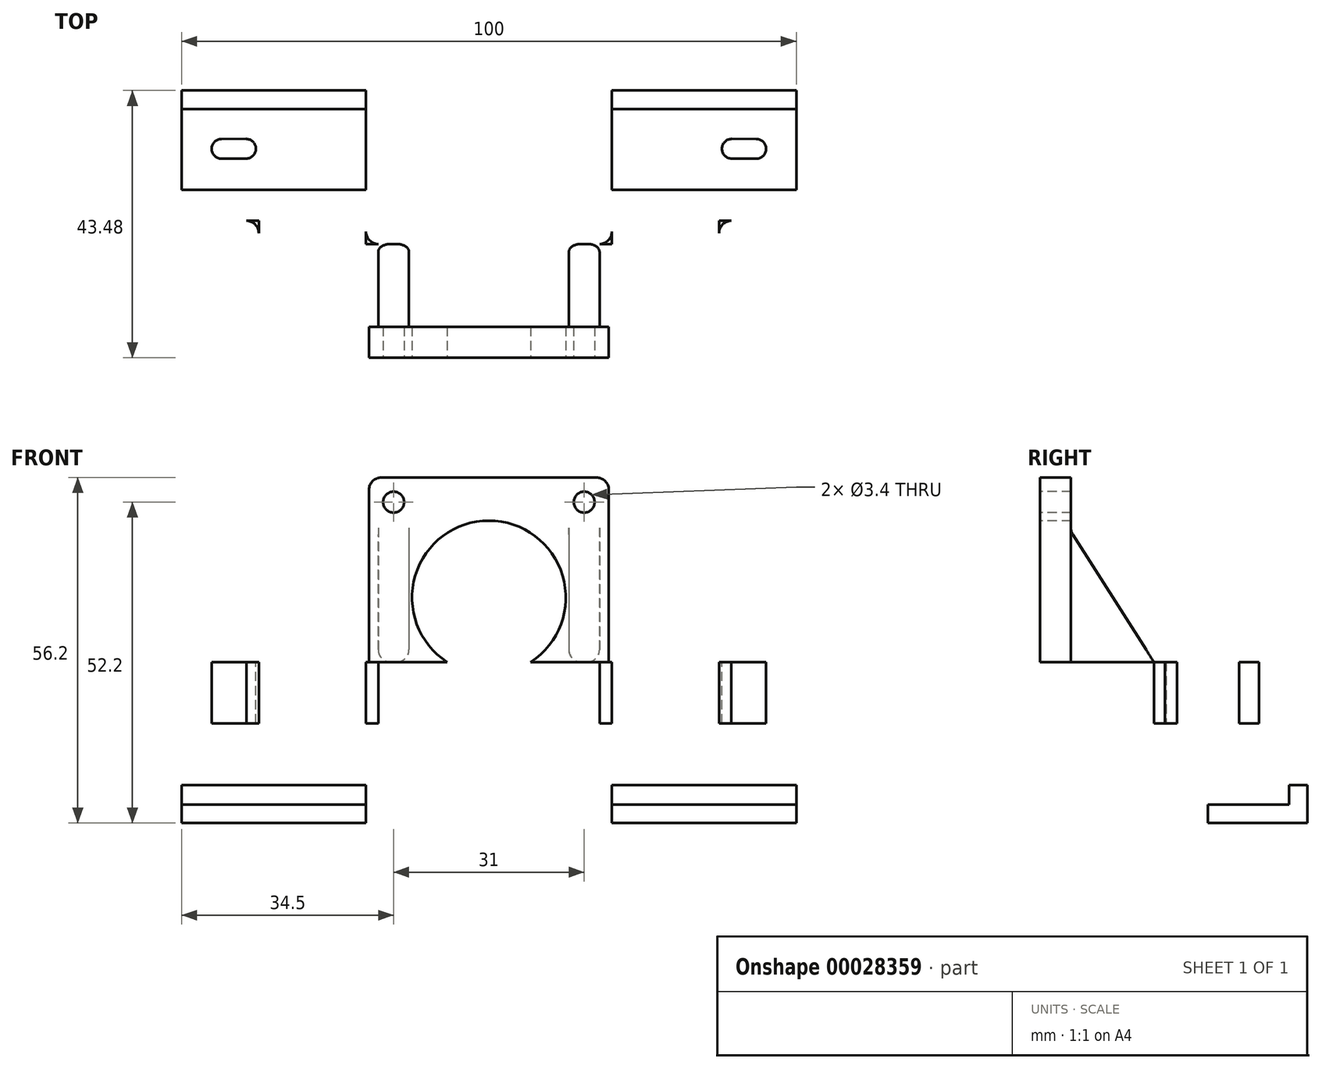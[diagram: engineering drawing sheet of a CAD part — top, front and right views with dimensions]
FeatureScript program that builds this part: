
annotation { "Feature Type Name" : "Feature", "Feature Type Description" : "" }
export const myFeature = defineFeature(function(context is Context, id is Id, definition is map)
    precondition{}
    {
        {
            var Q0;
            Q0=qCreatedBy(makeId("Top.planeOp"),FACE);
            var sketch = newSketch(context, id + "F0", { "sketchPlane" : qUnion([Q0])});
            skLineSegment(sketch, "E0", {"start": v(0, -13.82) * mm, "end": v(-37.44, -13.82) * mm});
            skLineSegment(sketch, "E1", {"start": v(-37.44, -13.82) * mm, "end": v(-37.44, 8.46) * mm});
            skLineSegment(sketch, "E2", {"start": v(-37.44, 8.46) * mm, "end": v(-50, 8.46) * mm});
            skLineSegment(sketch, "E3", {"start": v(-50, 8.46) * mm, "end": v(-50, 13.46) * mm});
            skLineSegment(sketch, "E4", {"start": v(-50, 13.46) * mm, "end": v(-20, 13.46) * mm});
            skLineSegment(sketch, "E5", {"start": v(-20, 13.46) * mm, "end": v(-20, 4.68) * mm});
            skLineSegment(sketch, "E6", {"start": v(-20, 4.68) * mm, "end": v(0, 4.68) * mm});
            skLineSegment(sketch, "E7", {"start": v(0, 4.68) * mm, "end": v(0, -13.82) * mm});
            skLineSegment(sketch, "E8.0", {"start": v(-18.87, 13.46) * mm, "end": v(-18.87, 4.68) * mm, "construction": true});
            skSolve(sketch);
        }
        {
            var Q0;
            Q0=qSketchRegion(id+"F0",true);
            extrude(context, id + "F1", {"entities" : qUnion([Q0]), "depth" : 10 * mm});
        }
        {
            var Q0;
            Q0=makeQuery(id+"F1.opExtrude","SWEPT_FACE",FACE,{"disambiguationData":[OSD([sQuery(id+"F0.wireOp",EDGE,"E0")])]});
            var sketch = newSketch(context, id + "F2", { "sketchPlane" : qUnion([Q0])});
            skLineSegment(sketch, "E9", {"start": v(0, 5) * mm, "end": v(0, 5) * mm});
            skCircle(sketch, "E10", {"center": v(-15.5, 5) * mm, "radius": 1.6 * mm});
            skSolve(sketch);
        }
        {
            var Q0;
            Q0=qSketchRegion(id+"F2",true);
            extrude(context, id + "F3", {"entities" : qUnion([Q0]), "operationType" : NewBodyOperationType.REMOVE, "endBound" : BoundingType.THROUGH_ALL, "oppositeDirection" : true, "depth" : 25 * mm});
        }
        {
            var Q0;
            {var subQ0=makeQuery(id+"F1.opExtrude","CAP_FACE",FACE,{"disambiguationData":[OSD([sQuery(id+"F0.wireOp",EDGE,"E0"),sQuery(id+"F0.wireOp",EDGE,"fd64a43a-5635-4f94-a977-4dd36923accb"),sQuery(id+"F0.wireOp",EDGE,"1334f7d4-4c90-4769-8fa3-fe5f576fb005"),sQuery(id+"F0.wireOp",EDGE,"E1"),sQuery(id+"F0.wireOp",EDGE,"E2"),sQuery(id+"F0.wireOp",EDGE,"E3"),sQuery(id+"F0.wireOp",EDGE,"E4"),sQuery(id+"F0.wireOp",EDGE,"E5"),sQuery(id+"F0.wireOp",EDGE,"E6"),sQuery(id+"F0.wireOp",EDGE,"E7")])],"isStart":false});Q0=makeQuery(id+"F22.boolean.opBoolean","MERGE",FACE,{"derivedFrom":[subQ0,makeQuery(id+"F22.opPattern","COPY",FACE,{"derivedFrom":subQ0,"instanceName":"1"})]});}
            var sketch = newSketch(context, id + "F4", { "sketchPlane" : qUnion([Q0])});
            skCircle(sketch, "E11", {"center": v(-30, 1.46) * mm, "radius": 4.1 * mm});
            skLineSegment(sketch, "E12", {"start": v(-30, 1.46) * mm, "end": v(-30, -13.82) * mm, "construction": true});
            skLineSegment(sketch, "E13.bottom", {"start": v(-30.49, -2.04) * mm, "end": v(-29.51, -2.04) * mm});
            skLineSegment(sketch, "E13.top", {"start": v(-30.49, -14.16) * mm, "end": v(-29.51, -14.16) * mm});
            skLineSegment(sketch, "E13.left", {"start": v(-30.49, -2.04) * mm, "end": v(-30.49, -14.16) * mm});
            skLineSegment(sketch, "E13.right", {"start": v(-29.51, -2.04) * mm, "end": v(-29.51, -14.16) * mm});
            skPoint(sketch, "E14", {"position": v(-30, -2.04) * mm});
            skSolve(sketch);
        }
        {
            var Q0;
            Q0=qSketchRegion(id+"F4",true);
            var Q1;
            {var subQ3=sQuery(id+"F4.wireOp",EDGE,"E13.bottom");Q1=makeQuery(id+"F4.imprint","IMPRINT",FACE,{"disambiguationData":[TD([[makeQuery(id+"F4.imprint","IMPRINT",EDGE,{"derivedFrom":subQ3}),-1.0]])]});}
            extrude(context, id + "F5", {"entities" : qUnion([Q0, Q1]), "operationType" : NewBodyOperationType.REMOVE, "endBound" : BoundingType.THROUGH_ALL, "oppositeDirection" : true, "depth" : 25 * mm});
        }
        {
            var Q0;
            Q0=makeQuery(id+"F1.opExtrude","SWEPT_FACE",FACE,{"disambiguationData":[OSD([sQuery(id+"F0.wireOp",EDGE,"E1")])]});
            var sketch = newSketch(context, id + "F6", { "sketchPlane" : qUnion([Q0])});
            skCircle(sketch, "E15", {"center": v(10.1, 4.98) * mm, "radius": 1.4 * mm});
            skCircle(sketch, "E16", {"center": v(10.1, 4.98) * mm, "radius": 1.7 * mm});
            skSolve(sketch);
        }
        {
            var Q0;
            Q0=makeQuery(id+"F6.imprint","IMPRINT",FACE,{"disambiguationData":[TD([[makeQuery(id+"F6.imprint","IMPRINT",EDGE,{"derivedFrom":sQuery(id+"F6.wireOp",EDGE,"E15")}),1.0]])]});
            extrude(context, id + "F7", {"entities" : qUnion([Q0]), "operationType" : NewBodyOperationType.REMOVE, "oppositeDirection" : true, "depth" : 18 * mm});
        }
        {
            var Q0;
            Q0=makeQuery(id+"F1.opExtrude","CAP_FACE",FACE,{"disambiguationData":[OSD([sQuery(id+"F0.wireOp",EDGE,"E0"),sQuery(id+"F0.wireOp",EDGE,"E1"),sQuery(id+"F0.wireOp",EDGE,"E2"),sQuery(id+"F0.wireOp",EDGE,"E3"),sQuery(id+"F0.wireOp",EDGE,"E4"),sQuery(id+"F0.wireOp",EDGE,"E5"),sQuery(id+"F0.wireOp",EDGE,"E6"),sQuery(id+"F0.wireOp",EDGE,"E7")])],"isStart":false});
            var sketch = newSketch(context, id + "F8", { "sketchPlane" : qUnion([Q0])});
            skLineSegment(sketch, "E17.0", {"start": v(-19.51, -2.61) * mm, "end": v(-19.51, -13.82) * mm, "construction": true});
            skLineSegment(sketch, "E18.bottom", {"start": v(-19.51, -13.82) * mm, "end": v(0, -13.82) * mm});
            skLineSegment(sketch, "E18.top", {"start": v(-19.51, -8.82) * mm, "end": v(0, -8.82) * mm});
            skLineSegment(sketch, "E18.left", {"start": v(-19.51, -13.82) * mm, "end": v(-19.51, -8.82) * mm});
            skLineSegment(sketch, "E18.right", {"start": v(0, -13.82) * mm, "end": v(0, -8.82) * mm});
            skSolve(sketch);
        }
        {
            var Q0;
            Q0=makeQuery(id+"F6.imprint","IMPRINT",FACE,{"disambiguationData":[TD([[makeQuery(id+"F6.imprint","IMPRINT",EDGE,{"derivedFrom":sQuery(id+"F6.wireOp",EDGE,"E15")}),1.0]])]});
            var Q1;
            Q1=makeQuery(id+"F6.imprint","IMPRINT",FACE,{"disambiguationData":[TD([[makeQuery(id+"F6.imprint","IMPRINT",EDGE,{"derivedFrom":sQuery(id+"F6.wireOp",EDGE,"E15")}),-1.0]])]});
            extrude(context, id + "F9", {"entities" : qUnion([Q0, Q1]), "operationType" : NewBodyOperationType.REMOVE, "endBound" : BoundingType.UP_TO_NEXT, "oppositeDirection" : true, "depth" : 25 * mm});
        }
        {
            var Q0;
            Q0=makeQuery(id+"F1.opExtrude","SWEPT_FACE",FACE,{"disambiguationData":[OSD([sQuery(id+"F0.wireOp",EDGE,"E3")])]});
            var sketch = newSketch(context, id + "F10", { "sketchPlane" : qUnion([Q0])});
            skLineSegment(sketch, "E19", {"start": v(-13.46, 0) * mm, "end": v(-26.66, 0) * mm});
            skLineSegment(sketch, "E20", {"start": v(-26.66, 0) * mm, "end": v(-26.66, -13.2) * mm});
            skLineSegment(sketch, "E21", {"start": v(-29.66, -13.2) * mm, "end": v(-29.66, 10) * mm});
            skLineSegment(sketch, "E22", {"start": v(-29.66, 10) * mm, "end": v(-13.46, 10) * mm});
            skLineSegment(sketch, "E23", {"start": v(-26.66, -13.2) * mm, "end": v(-13.46, -13.2) * mm});
            skLineSegment(sketch, "E24", {"start": v(-13.46, -13.2) * mm, "end": v(-13.46, -16.2) * mm});
            skLineSegment(sketch, "E25", {"start": v(-13.46, -16.2) * mm, "end": v(-29.66, -16.2) * mm});
            skLineSegment(sketch, "E26", {"start": v(-29.66, -16.2) * mm, "end": v(-29.66, -13.2) * mm});
            skSolve(sketch);
        }
        {
            var Q0;
            Q0=makeQuery(id+"F10.imprint","IMPRINT",FACE,{"disambiguationData":[TD([[makeQuery(id+"F10.imprint","IMPRINT",EDGE,{"derivedFrom":sQuery(id+"F10.wireOp",EDGE,"E19")}),-1.0]])]});
            var Q1;
            Q1=makeQuery(id+"F1.opExtrude","SWEPT_FACE",FACE,{"disambiguationData":[OSD([sQuery(id+"F0.wireOp",EDGE,"E5")])]});
            extrude(context, id + "F11", {"entities" : qUnion([Q0]), "operationType" : NewBodyOperationType.ADD, "endBound" : BoundingType.UP_TO_SURFACE, "oppositeDirection" : true, "endBoundEntityFace" : qUnion([Q1]), "depth" : 25 * mm});
        }
        {
            var Q0;
            {var subQ0=makeQuery(id+"F1.opExtrude","CAP_FACE",FACE,{"disambiguationData":[OSD([sQuery(id+"F0.wireOp",EDGE,"E0"),sQuery(id+"F0.wireOp",EDGE,"E1"),sQuery(id+"F0.wireOp",EDGE,"E2"),sQuery(id+"F0.wireOp",EDGE,"E3"),sQuery(id+"F0.wireOp",EDGE,"E4"),sQuery(id+"F0.wireOp",EDGE,"E5"),sQuery(id+"F0.wireOp",EDGE,"E6"),sQuery(id+"F0.wireOp",EDGE,"E7")])],"isStart":false});Q0=makeQuery(id+"F11.boolean.opBoolean","MERGE",FACE,{"derivedFrom":[subQ0,makeQuery(id+"F22.opPattern","COPY",FACE,{"derivedFrom":subQ0,"instanceName":"1"}),makeQuery(id+"F11.opExtrude","SWEPT_FACE",FACE,{"disambiguationData":[OSD([sQuery(id+"F10.wireOp",EDGE,"E22")])]})]});}
            var sketch = newSketch(context, id + "F12", { "sketchPlane" : qUnion([Q0])});
            skLineSegment(sketch, "E27", {"start": v(-50, 20.16) * mm, "end": v(-43.5, 20.16) * mm, "construction": true});
            skLineSegment(sketch, "E28.0", {"start": v(-43.5, 20.16) * mm, "end": v(-39.5, 20.17) * mm});
            skArc(sketch, "E29.0.startCap", {"start": v(-43.5, 18.56) * mm, "mid": v(-45.1, 20.15) * mm, "end": v(-43.5, 21.76) * mm});
            skArc(sketch, "E29.0.endCap", {"start": v(-39.51, 21.77) * mm, "mid": v(-37.9, 20.18) * mm, "end": v(-39.5, 18.57) * mm});
            skLineSegment(sketch, "E29.0.left", {"start": v(-43.5, 21.76) * mm, "end": v(-39.51, 21.77) * mm});
            skLineSegment(sketch, "E29.0.right", {"start": v(-43.5, 18.56) * mm, "end": v(-39.5, 18.57) * mm});
            skSolve(sketch);
        }
        {
            var Q0;
            {var subQ8=sQuery(id+"F8.wireOp",EDGE,"E18.left");Q0=makeQuery(id+"F8.imprint","IMPRINT",FACE,{"disambiguationData":[TD([[makeQuery(id+"F8.imprint","IMPRINT",EDGE,{"derivedFrom":subQ8}),-1.0]])]});}
            var Q1;
            {var subQ5=sQuery(id+"F8.wireOp",EDGE,"E18.right");Q1=makeQuery(id+"F8.imprint","IMPRINT",FACE,{"disambiguationData":[TD([[makeQuery(id+"F8.imprint","IMPRINT",EDGE,{"derivedFrom":subQ5}),1.0]])]});}
            extrude(context, id + "F13", {"entities" : qUnion([Q0, Q1]), "operationType" : NewBodyOperationType.ADD, "depth" : 30 * mm});
        }
        {
            var Q0;
            {var subQ0=sQuery(id+"F0.wireOp",EDGE,"E0");var subQ1=sQuery(id+"F0.wireOp",EDGE,"E7");var subQ8=makeQuery(id+"F13.boolean.opBoolean","MERGE",FACE,{"derivedFrom":[makeQuery(id+"F5.boolean.opBoolean","SPLIT",FACE,{"disambiguationData":[TD([makeQuery(id+"F1.opExtrude","SWEPT_FACE",FACE,{"disambiguationData":[OSD([subQ1])]})])],"derivedFrom":makeQuery(id+"F1.opExtrude","SWEPT_FACE",FACE,{"disambiguationData":[OSD([subQ0])]})}),makeQuery(id+"F13.opExtrude","SWEPT_FACE",FACE,{"disambiguationData":[OSD([sQuery(id+"F8.wireOp",EDGE,"E18.bottom")])]})]});Q0=makeQuery(id+"F22.boolean.opBoolean","MERGE",FACE,{"derivedFrom":[subQ8,makeQuery(id+"F22.opPattern","COPY",FACE,{"derivedFrom":subQ8,"instanceName":"1"})]});}
            var sketch = newSketch(context, id + "F14", { "sketchPlane" : qUnion([Q0])});
            skLineSegment(sketch, "E30.0", {"start": v(29.51, 36) * mm, "end": v(-29.51, 36) * mm, "construction": true});
            skCircle(sketch, "E31", {"center": v(-15.5, 36) * mm, "radius": 1.7 * mm});
            skCircle(sketch, "E32.0", {"center": v(-15.5, 5) * mm, "radius": 1.6 * mm});
            skSolve(sketch);
        }
        {
            var Q0;
            Q0=makeQuery(id+"F14.imprint","IMPRINT",FACE,{"disambiguationData":[TD([[makeQuery(id+"F14.imprint","IMPRINT",EDGE,{"derivedFrom":sQuery(id+"F14.wireOp",EDGE,"E31")}),1.0]])]});
            extrude(context, id + "F15", {"entities" : qUnion([Q0]), "operationType" : NewBodyOperationType.REMOVE, "oppositeDirection" : true, "depth" : 25 * mm});
        }
        {
            var Q0;
            Q0=makeQuery(id+"F1.opExtrude","SWEPT_EDGE",EDGE,{"disambiguationData":[OSD([sQuery(id+"F0.wireOp",EDGE,"E0"),sQuery(id+"F0.wireOp",EDGE,"E1")])]});
            var Q1;
            Q1=makeQuery(id+"F1.opExtrude","SWEPT_EDGE",EDGE,{"disambiguationData":[OSD([sQuery(id+"F0.wireOp",EDGE,"E1"),sQuery(id+"F0.wireOp",EDGE,"E2")])]});
            var Q2;
            Q2=makeQuery(id+"F1.opExtrude","SWEPT_EDGE",EDGE,{"disambiguationData":[OSD([sQuery(id+"F0.wireOp",EDGE,"E2"),sQuery(id+"F0.wireOp",EDGE,"E3")])]});
            var Q3;
            Q3=makeQuery(id+"F13.opExtrude","CAP_EDGE",EDGE,{"disambiguationData":[OSD([sQuery(id+"F8.wireOp",EDGE,"E18.left")])],"isStart":true});
            var Q4;
            Q4=makeQuery(id+"F13.opExtrude","CAP_EDGE",EDGE,{"disambiguationData":[OSD([sQuery(id+"F8.wireOp",EDGE,"E18.left")])],"isStart":false});
            var Q5;
            Q5=makeQuery(id+"F1.opExtrude","SWEPT_EDGE",EDGE,{"disambiguationData":[OSD([sQuery(id+"F0.wireOp",EDGE,"E5"),sQuery(id+"F0.wireOp",EDGE,"E6")])]});
            fillet(context, id + "F16", {"entities" : qUnion([Q0, Q1, Q2, Q3, Q4, Q5]), "radius" : 2 * mm, "tangentPropagation" : true, "allowEdgeOverflow" : false});
        }
        {
            var Q0;
            {var subQ0=sQuery(id+"F0.wireOp",EDGE,"E0");var subQ1=sQuery(id+"F0.wireOp",EDGE,"E1");var subQ2=sQuery(id+"F0.wireOp",EDGE,"E2");var subQ3=sQuery(id+"F0.wireOp",EDGE,"E3");var subQ4=sQuery(id+"F0.wireOp",EDGE,"E4");var subQ5=sQuery(id+"F0.wireOp",EDGE,"E5");var subQ6=sQuery(id+"F0.wireOp",EDGE,"E6");var subQ7=sQuery(id+"F0.wireOp",EDGE,"E7");var subQ8=makeQuery(id+"F1.opExtrude","CAP_FACE",FACE,{"disambiguationData":[OSD([subQ0,subQ1,subQ2,subQ3,subQ4,subQ5,subQ6,subQ7])],"isStart":false});var subQ9=sQuery(id+"F10.wireOp",EDGE,"E22");var subQ10=makeQuery(id+"F11.boolean.opBoolean","MERGE",FACE,{"derivedFrom":[subQ8,makeQuery(id+"F11.opExtrude","SWEPT_FACE",FACE,{"disambiguationData":[OSD([subQ9])]})]});Q0=makeQuery(id+"F23.boolean.opBoolean","SPLIT",FACE,{"disambiguationData":[TD([makeQuery(id+"F1.opExtrude","SWEPT_FACE",FACE,{"disambiguationData":[OSD([subQ1])]})])],"derivedFrom":makeQuery(id+"F22.boolean.opBoolean","MERGE",FACE,{"derivedFrom":[subQ10,makeQuery(id+"F22.opPattern","COPY",FACE,{"derivedFrom":subQ10,"instanceName":"1"})]})});}
            var sketch = newSketch(context, id + "F17", { "sketchPlane" : qUnion([Q0])});
            skLineSegment(sketch, "E33", {"start": v(-18, 4.68) * mm, "end": v(-18, -8.82) * mm});
            skLineSegment(sketch, "E34", {"start": v(-18, 4.68) * mm, "end": v(-13, 4.68) * mm});
            skLineSegment(sketch, "E35", {"start": v(-13, 4.68) * mm, "end": v(-13, -8.82) * mm});
            skLineSegment(sketch, "E36", {"start": v(-13, -8.82) * mm, "end": v(-18, -8.82) * mm});
            skSolve(sketch);
        }
        {
            var Q0;
            Q0=makeQuery(id+"F12.imprint","IMPRINT",FACE,{"disambiguationData":[TD([[makeQuery(id+"F12.imprint","IMPRINT",EDGE,{"derivedFrom":sQuery(id+"F12.wireOp",EDGE,"E29.0.startCap")}),-1.0]])]});
            extrude(context, id + "F18", {"entities" : qUnion([Q0]), "operationType" : NewBodyOperationType.REMOVE, "oppositeDirection" : true, "depth" : 20 * mm});
        }
        {
            var Q0;
            Q0=makeQuery(id+"F17.imprint","IMPRINT",FACE,{"disambiguationData":[TD([[makeQuery(id+"F17.imprint","IMPRINT",EDGE,{"derivedFrom":sQuery(id+"F17.wireOp",EDGE,"E33")}),1.0]])]});
            extrude(context, id + "F19", {"entities" : qUnion([Q0]), "operationType" : NewBodyOperationType.ADD, "depth" : 22 * mm});
        }
        {
            var Q0;
            Q0=makeQuery(id+"F19.opExtrude","CAP_EDGE",EDGE,{"disambiguationData":[OSD([sQuery(id+"F17.wireOp",EDGE,"E34")])],"isStart":false});
            chamfer(context, id + "F20", {"entities" : qUnion([Q0]), "chamferType" : ChamferType.TWO_OFFSETS, "width1" : 22 * mm, "oppositeDirection" : false, "width2" : 14 * mm});
        }
        {
            var Q0;
            {var subQ0=sQuery(id+"F0.wireOp",EDGE,"E0");var subQ1=sQuery(id+"F0.wireOp",EDGE,"E7");var subQ8=makeQuery(id+"F13.boolean.opBoolean","MERGE",FACE,{"derivedFrom":[makeQuery(id+"F5.boolean.opBoolean","SPLIT",FACE,{"disambiguationData":[TD([makeQuery(id+"F1.opExtrude","SWEPT_FACE",FACE,{"disambiguationData":[OSD([subQ1])]})])],"derivedFrom":makeQuery(id+"F1.opExtrude","SWEPT_FACE",FACE,{"disambiguationData":[OSD([subQ0])]})}),makeQuery(id+"F13.opExtrude","SWEPT_FACE",FACE,{"disambiguationData":[OSD([sQuery(id+"F8.wireOp",EDGE,"E18.bottom")])]})]});Q0=makeQuery(id+"F22.boolean.opBoolean","MERGE",FACE,{"derivedFrom":[subQ8,makeQuery(id+"F22.opPattern","COPY",FACE,{"derivedFrom":subQ8,"instanceName":"1"})]});}
            var sketch = newSketch(context, id + "F21", { "sketchPlane" : qUnion([Q0])});
            skCircle(sketch, "E37", {"center": v(0, 20.48) * mm, "radius": 12.5 * mm});
            skLineSegment(sketch, "E38.0", {"start": v(0, 37.65) * mm, "end": v(0, 3.31) * mm, "construction": true});
            skSolve(sketch);
        }
        {
            var Q0;
            Q0=makeQuery(id+"F1.opExtrude","SWEPT_BODY",BODY,{"disambiguationData":[OSD([sQuery(id+"F0.wireOp",EDGE,"E0"),sQuery(id+"F0.wireOp",EDGE,"fd64a43a-5635-4f94-a977-4dd36923accb"),sQuery(id+"F0.wireOp",EDGE,"1334f7d4-4c90-4769-8fa3-fe5f576fb005"),sQuery(id+"F0.wireOp",EDGE,"E1"),sQuery(id+"F0.wireOp",EDGE,"E2"),sQuery(id+"F0.wireOp",EDGE,"E3"),sQuery(id+"F0.wireOp",EDGE,"E4"),sQuery(id+"F0.wireOp",EDGE,"E5"),sQuery(id+"F0.wireOp",EDGE,"E6"),sQuery(id+"F0.wireOp",EDGE,"E7")])]});
            var Q1;
            Q1=qCreatedBy(makeId("Right.planeOp"),FACE);
            mirror(context, id + "F22", {"operationType" : NewBodyOperationType.ADD, "entities" : qUnion([Q0]), "mirrorPlane" : qUnion([Q1])});
        }
        {
            var Q0;
            Q0=qSketchRegion(id+"F21",true);
            var Q1;
            Q1=makeQuery(id+"F21.imprint","IMPRINT",FACE,{"disambiguationData":[TD([[makeQuery(id+"F21.imprint","IMPRINT",EDGE,{"derivedFrom":sQuery(id+"F21.wireOp",EDGE,"E37")}),1.0]])]});
            extrude(context, id + "F23", {"entities" : qUnion([Q0, Q1]), "operationType" : NewBodyOperationType.REMOVE, "oppositeDirection" : true, "depth" : 25 * mm});
        }
        {
            var Q0;
            Q0=makeQuery(id+"F22.opPattern","COPY",EDGE,{"derivedFrom":makeQuery(id+"F20.opChamfer","BLEND_EDGE",EDGE,{"blendedFrom":[makeQuery(id+"F19.opExtrude","CAP_EDGE",EDGE,{"disambiguationData":[OSD([sQuery(id+"F17.wireOp",EDGE,"E34")])],"isStart":false}),makeQuery(id+"F13.opExtrude","SWEPT_FACE",FACE,{"disambiguationData":[OSD([sQuery(id+"F8.wireOp",EDGE,"E18.top")])]})],"blendedInto":[makeQuery(id+"F13.opExtrude","SWEPT_FACE",FACE,{"disambiguationData":[OSD([sQuery(id+"F8.wireOp",EDGE,"E18.top")])]})]}),"instanceName":"1"});
            var Q1;
            Q1=makeQuery(id+"F20.opChamfer","BLEND_EDGE",EDGE,{"blendedFrom":[makeQuery(id+"F19.opExtrude","CAP_EDGE",EDGE,{"disambiguationData":[OSD([sQuery(id+"F17.wireOp",EDGE,"E34")])],"isStart":false}),makeQuery(id+"F13.opExtrude","SWEPT_FACE",FACE,{"disambiguationData":[OSD([sQuery(id+"F8.wireOp",EDGE,"E18.top")])]})],"blendedInto":[makeQuery(id+"F13.opExtrude","SWEPT_FACE",FACE,{"disambiguationData":[OSD([sQuery(id+"F8.wireOp",EDGE,"E18.top")])]})]});
            var Q2;
            Q2=makeQuery(id+"F19.opExtrude","CAP_EDGE",EDGE,{"disambiguationData":[OSD([sQuery(id+"F17.wireOp",EDGE,"E33")])],"isStart":true});
            var Q3;
            Q3=makeQuery(id+"F19.opExtrude","CAP_EDGE",EDGE,{"disambiguationData":[OSD([sQuery(id+"F17.wireOp",EDGE,"E35")])],"isStart":true});
            var Q4;
            Q4=makeQuery(id+"F22.opPattern","COPY",EDGE,{"derivedFrom":makeQuery(id+"F19.opExtrude","CAP_EDGE",EDGE,{"disambiguationData":[OSD([sQuery(id+"F17.wireOp",EDGE,"E35")])],"isStart":true}),"instanceName":"1"});
            var Q5;
            Q5=makeQuery(id+"F22.opPattern","COPY",EDGE,{"derivedFrom":makeQuery(id+"F19.opExtrude","CAP_EDGE",EDGE,{"disambiguationData":[OSD([sQuery(id+"F17.wireOp",EDGE,"E33")])],"isStart":true}),"instanceName":"1"});
            var Q6;
            Q6=makeQuery(id+"F22.opPattern","COPY",EDGE,{"derivedFrom":makeQuery(id+"F19.opExtrude","SWEPT_EDGE",EDGE,{"disambiguationData":[OSD([sQuery(id+"F8.wireOp",EDGE,"E18.top"),sQuery(id+"F17.wireOp",EDGE,"E33"),sQuery(id+"F17.wireOp",EDGE,"E36")])]}),"instanceName":"1"});
            var Q7;
            Q7=makeQuery(id+"F19.opExtrude","SWEPT_EDGE",EDGE,{"disambiguationData":[OSD([sQuery(id+"F8.wireOp",EDGE,"E18.top"),sQuery(id+"F17.wireOp",EDGE,"E33"),sQuery(id+"F17.wireOp",EDGE,"E36")])]});
            var Q8;
            Q8=makeQuery(id+"F22.opPattern","COPY",EDGE,{"derivedFrom":makeQuery(id+"F19.opExtrude","SWEPT_EDGE",EDGE,{"disambiguationData":[OSD([sQuery(id+"F8.wireOp",EDGE,"E18.top"),sQuery(id+"F17.wireOp",EDGE,"E35"),sQuery(id+"F17.wireOp",EDGE,"E36")])]}),"instanceName":"1"});
            var Q9;
            Q9=makeQuery(id+"F19.opExtrude","SWEPT_EDGE",EDGE,{"disambiguationData":[OSD([sQuery(id+"F8.wireOp",EDGE,"E18.top"),sQuery(id+"F17.wireOp",EDGE,"E35"),sQuery(id+"F17.wireOp",EDGE,"E36")])]});
            fillet(context, id + "F24", {"entities" : qUnion([Q0, Q1, Q2, Q3, Q4, Q5, Q6, Q7, Q8, Q9]), "radius" : 2 * mm, "tangentPropagation" : true, "allowEdgeOverflow" : false});
        }
    });
